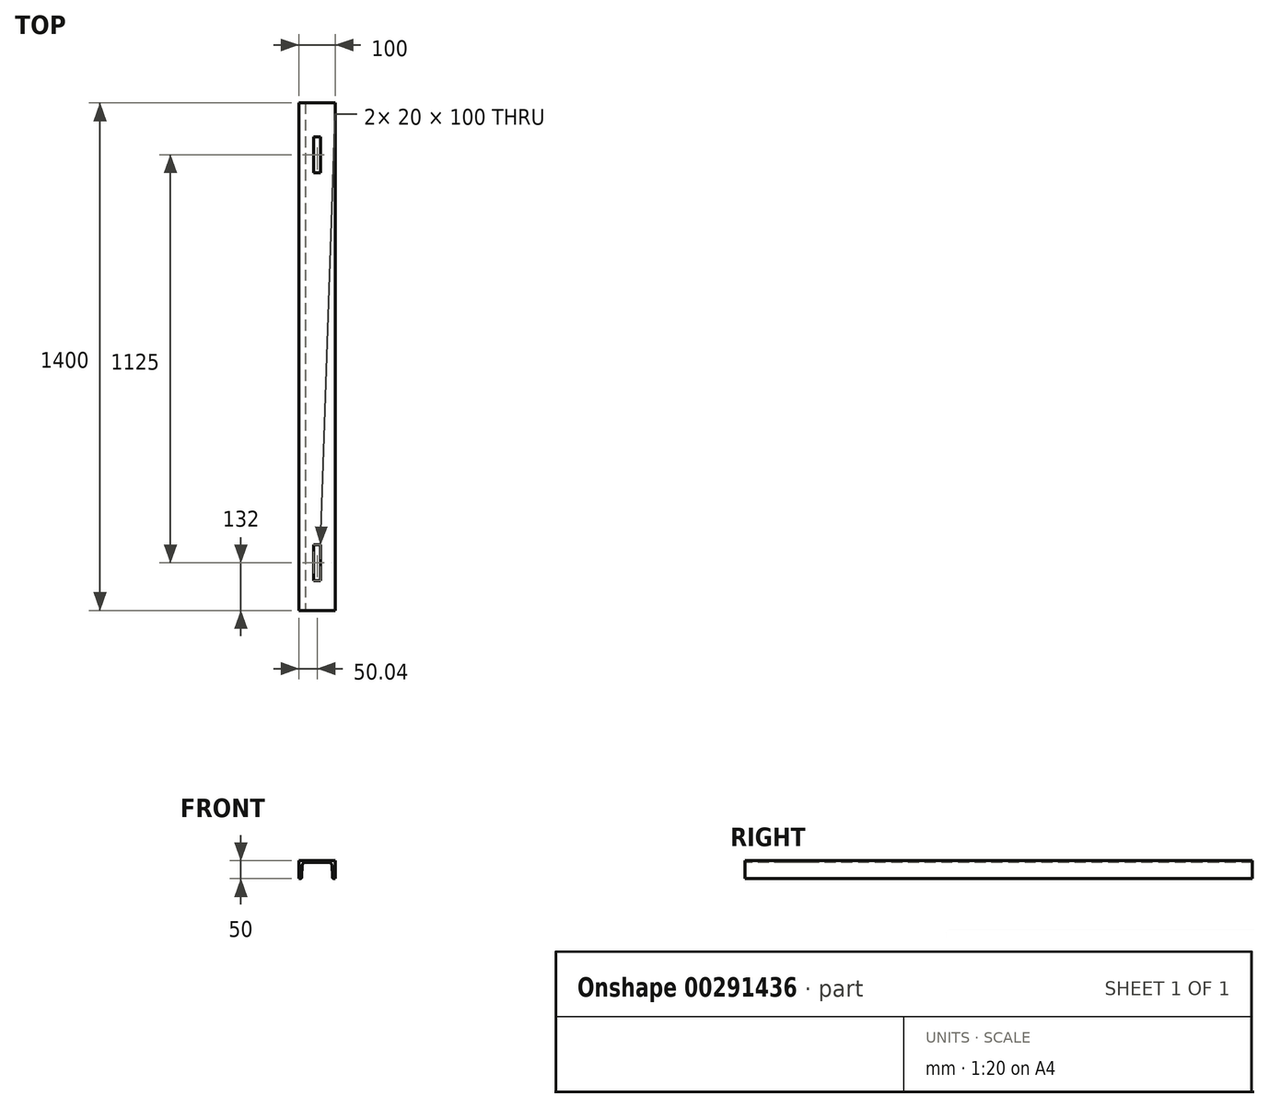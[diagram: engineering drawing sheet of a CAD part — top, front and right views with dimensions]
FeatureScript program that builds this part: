
annotation { "Feature Type Name" : "Feature", "Feature Type Description" : "" }
export const myFeature = defineFeature(function(context is Context, id is Id, definition is map)
    precondition{}
    {
        {
            var Q0;
            Q0=qCreatedBy(makeId("Front.planeOp"),FACE);
            var sketch = newSketch(context, id + "F0", { "sketchPlane" : qUnion([Q0])});
            skLineSegment(sketch, "E0", {"start": v(-50.04, 35.77) * mm, "end": v(49.96, 35.77) * mm});
            skLineSegment(sketch, "E1", {"start": v(49.96, 35.77) * mm, "end": v(49.96, -14.23) * mm});
            skLineSegment(sketch, "E2", {"start": v(49.96, -14.23) * mm, "end": v(46.28, -14.23) * mm});
            skLineSegment(sketch, "E3", {"start": v(42.28, -10.42) * mm, "end": v(40.67, 23.16) * mm});
            skArc(sketch, "E4.filletArc", {"start": v(42.28, -10.42) * mm, "mid": v(43.52, -13.12) * mm, "end": v(46.28, -14.23) * mm});
            skArc(sketch, "E5.filletArc", {"start": v(40.67, 23.16) * mm, "mid": v(38.2, 28.56) * mm, "end": v(32.68, 30.77) * mm});
            skArc(sketch, "E6.MirrorCS", {"start": v(-40.75, 23.16) * mm, "mid": v(-38.23, 28.61) * mm, "end": v(-32.62, 30.77) * mm});
            skLineSegment(sketch, "E7.MirrorCS", {"start": v(-50.04, 35.77) * mm, "end": v(-50.04, -14.23) * mm});
            skLineSegment(sketch, "E8.MirrorCS", {"start": v(-42.36, -10.42) * mm, "end": v(-40.75, 23.16) * mm});
            skArc(sketch, "E9.MirrorCS", {"start": v(-42.36, -10.42) * mm, "mid": v(-43.6, -13.12) * mm, "end": v(-46.35, -14.23) * mm});
            skLineSegment(sketch, "E10.MirrorCS", {"start": v(-50.04, -14.23) * mm, "end": v(-46.35, -14.23) * mm});
            skLineSegment(sketch, "E11", {"start": v(-32.62, 30.77) * mm, "end": v(32.68, 30.77) * mm});
            skSolve(sketch);
        }
        {
            var Q0;
            Q0=makeQuery(id+"F0.imprint","IMPRINT",FACE,{"disambiguationData":[TD([[makeQuery(id+"F0.imprint","IMPRINT",EDGE,{"derivedFrom":sQuery(id+"F0.wireOp",EDGE,"E0")}),-1.0]])]});
            extrude(context, id + "F1", {"entities" : qUnion([Q0]), "oppositeDirection" : true, "depth" : 1400 * mm});
        }
        {
            var Q0;
            Q0=makeQuery(id+"F1.opExtrude","SWEPT_FACE",FACE,{"disambiguationData":[OSD([sQuery(id+"F0.wireOp",EDGE,"E0")])]});
            var sketch = newSketch(context, id + "F2", { "sketchPlane" : qUnion([Q0])});
            skLineSegment(sketch, "E12.bottom", {"start": v(10, 182) * mm, "end": v(-10, 182) * mm});
            skLineSegment(sketch, "E12.top", {"start": v(10, 82) * mm, "end": v(-10, 82) * mm});
            skLineSegment(sketch, "E12.left", {"start": v(10, 182) * mm, "end": v(10, 82) * mm});
            skLineSegment(sketch, "E12.right", {"start": v(-10, 182) * mm, "end": v(-10, 82) * mm});
            skPoint(sketch, "E12.middle", {"position": v(0, 132) * mm});
            skLineSegment(sketch, "E13", {"start": v(0, 0) * mm, "end": v(0, 12.73) * mm, "construction": true});
            skLineSegment(sketch, "E14", {"start": v(-10, 1307) * mm, "end": v(-10, 1207) * mm});
            skLineSegment(sketch, "E15", {"start": v(-10, 1207) * mm, "end": v(10, 1207) * mm});
            skLineSegment(sketch, "E16", {"start": v(10, 1207) * mm, "end": v(10, 1307) * mm});
            skLineSegment(sketch, "E17", {"start": v(-10, 1307) * mm, "end": v(10, 1307) * mm});
            skSolve(sketch);
        }
        {
            var Q0;
            Q0=makeQuery(id+"F2.imprint","IMPRINT",FACE,{"disambiguationData":[TD([[makeQuery(id+"F2.imprint","IMPRINT",EDGE,{"derivedFrom":sQuery(id+"F2.wireOp",EDGE,"E12.bottom")}),1.0]])]});
            var Q1;
            Q1=makeQuery(id+"F2.imprint","IMPRINT",FACE,{"disambiguationData":[TD([[makeQuery(id+"F2.imprint","IMPRINT",EDGE,{"derivedFrom":sQuery(id+"F2.wireOp",EDGE,"E14")}),1.0]])]});
            extrude(context, id + "F3", {"entities" : qUnion([Q0, Q1]), "operationType" : NewBodyOperationType.REMOVE, "endBound" : BoundingType.UP_TO_NEXT, "oppositeDirection" : true, "depth" : 25 * mm});
        }
    });
